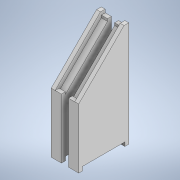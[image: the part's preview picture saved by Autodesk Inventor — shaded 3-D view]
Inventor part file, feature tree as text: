
AUTODESK INVENTOR PART (.ipt)
format: ipt  version: 2022.2 (Build 262287010, 287A)  size: 152,064 bytes
history: native  units: in
note: dims shown in document units (in); Inventor stores cm internally (conversion verified against a paired STEP export)
features: extrude x3, sketch x3, other x1, plane x1, mirror x1
ambient origin geometry x8: Origin, YZ Plane, XZ Plane, XY Plane, X Axis, Y Axis, Z Axis, Center Point
bodies: Body1 (feature_tree)
feature tree (9):
  other  "Sólido1"
  extrude  "Extrusión1"  Depth=0.1969in TaperAngle=0.0deg
  extrude  "Extrusión2"  Depth=5.2705in
  plane  "Plano de trabajo1"
  mirror  "Simetría1"
  extrude  "Extrusión3"  Depth=0.1969in
  sketch  "Boceto1"  dims[d11=0.315in d12=0.0in d16=0.1969in d17=0.0in]
  sketch  "Boceto2"  dims[d18=5.2705in d22=0.1772in]
  sketch  "Boceto4"  dims[d23=0.1969in d24=0.1969in d25=0.1969in d26=0.0in d27=0.0in d13=0.0197in d14=0.0344in]
